# Revit family: LeL Colorado 7.1
name_source: partatom
category: Lighting Fixtures
units: mm (PartAtom-declared; Revit-internal decimal feet)

## family parameters
Cut with Voids When Loaded = Yes
Host = Face
Light Source = No
Part Type = Normal
Room Calculation Point = No
Round Connector Dimension = Use Diameter
Shared = No

## types (5) — shared parameters
Accessories = WCCA11A0T
Alimentazione = 230 V
Apparent Load = 64 VA
CCT = 3500 K
CRI = 80
Default Elevation = 1219 mm
Description = Outdoor Linear Profile
Finish = LeL Black
IK = IK10
IP = IP65 IP67 IP69
Lamp = LED
Lenght = 925 mm  [stored 3.03478 ft]
Manufacturer = L&L Luce&Light
Model = CA71
Outercasing = 969 mm
Rated Power supply = 230 V
URL = https://www.lucelight.it
Wattage = 64 W
Weight = 8.50 kg

## per-type parameters (varying)
| type | Optic |
| 7.1 W 16°x66° 64W | COLORADO Light source : 7.1 W 16°x66° 64W |
| 7.1 D 64W | COLORADO Light source : 7.1 D 64W |
| 7.1 M 26° 64W | COLORADO Light source : 7.1 M 26° 64W |
| 7.1 S 16° 64W | COLORADO Light source : 7.1 S 16° 64W |
| 7.1 L 36° 64W | COLORADO Light source : 7.1 L 36° 64W |

note: [stored X ft] marks values corroborated as IEEE doubles in the binary element streams (Revit-internal decimal feet)

## geometry (parser evidence)
native form markers: Sweep x2
no freeform markers — native parametric forms only
